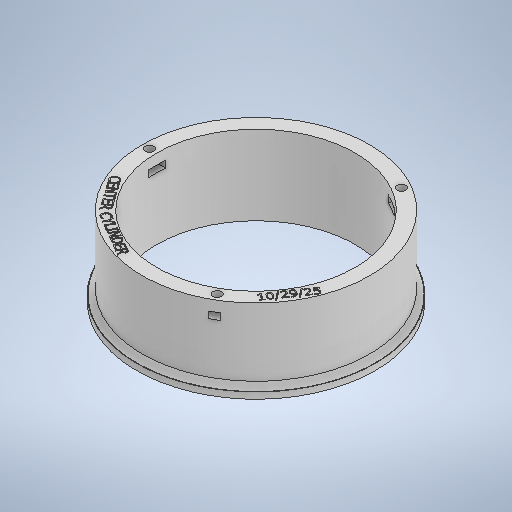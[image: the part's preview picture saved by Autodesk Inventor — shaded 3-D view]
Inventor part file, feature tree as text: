
AUTODESK INVENTOR PART (.ipt)
format: ipt  version: 2025 (Build 290162000, 162)  size: 757,760 bytes
history: native  units: mm
features: sketch x6, extrude x4, pattern_circular x2, hole x1, chamfer x1, emboss x1
ambient origin geometry x8: Origin, YZ Plane, XZ Plane, XY Plane, X Axis, Y Axis, Z Axis, Center Point
bodies: Solid1 (feature_tree)
feature tree (15):
  extrude  "Base"  Depth=30.0mm TaperAngle=0.0deg
  extrude  "Nut Seat"  Depth=108.9mm
  pattern_circular  "Circular Pattern1"  Count=3 Angle=360.0deg
  extrude  "Top Slice"  Depth=51.0mm
  hole  "Hole1"  [1 undecoded]
  pattern_circular  "Circular Pattern2"  Angle=45.0deg  [1 undecoded]
  extrude  "Lip"  Depth=1.0mm TaperAngle=0.0deg
  chamfer  "Chamfer 1"  Distance=0.5mm
  emboss  "Emboss1"
  sketch  "Sketch1"  dims[d0=102.0mm d3=30.0mm d4=0.0mm]
  sketch  "Sketch2"  dims[d6=95.1mm d7=108.9mm]
  sketch  "Sketch3"  dims[d8=3.2mm d9=0.0mm d10=30.0mm d11=360.0deg]
  sketch  "Sketch4"  dims[d13=5.0mm d14=0.0mm]
  sketch  "Sketch5"  dims[d15=4.2mm d16=6.0mm d17=4.0mm d18=2.0mm d19=90.0deg d20=8.0mm d21=0.0mm d22=51.0mm]
  sketch  "Sketch6"  dims[d23=30.0mm d24=360.0deg d26=3.0mm d27=0.0mm d31=2.5mm d32=2.0mm d33=45.0deg d34=1.0mm d35=0.0mm d12=0.5mm]
note: 2 required parameter values undecoded (feature->parameter linkage not recoverable at this tier; creation-order binding heuristic only, values carry confidence <= 0.55)
